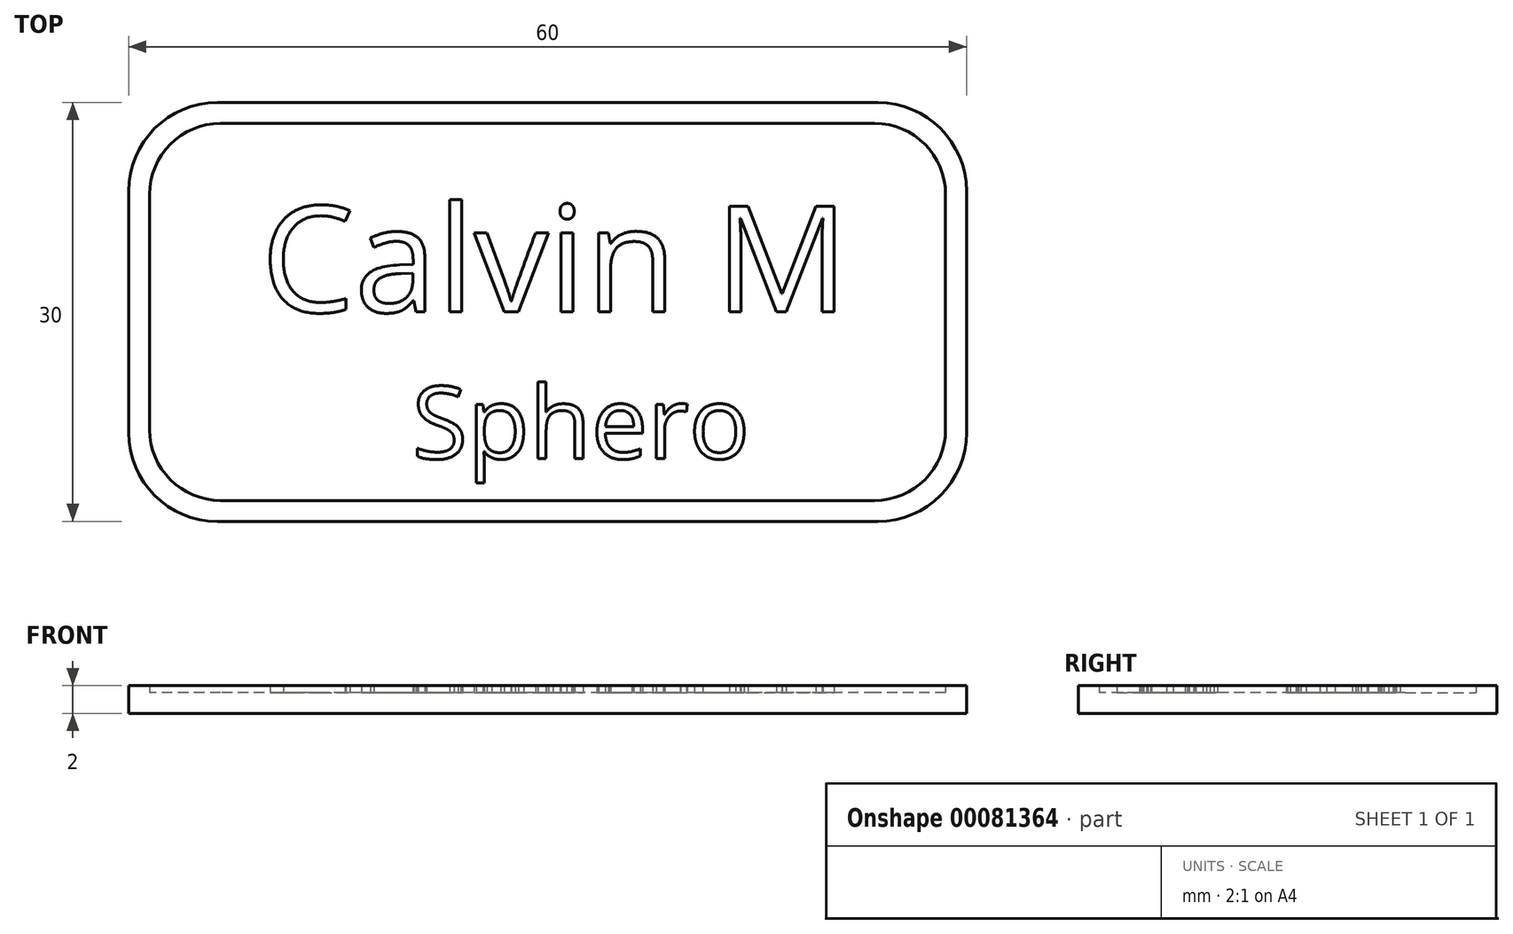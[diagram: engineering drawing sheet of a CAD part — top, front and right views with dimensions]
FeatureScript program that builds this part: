
annotation { "Feature Type Name" : "Feature", "Feature Type Description" : "" }
export const myFeature = defineFeature(function(context is Context, id is Id, definition is map)
    precondition{}
    {
        {
            var Q0;
            Q0=qCreatedBy(makeId("Top.planeOp"),FACE);
            var sketch = newSketch(context, id + "F0", { "sketchPlane" : qUnion([Q0])});
            skLineSegment(sketch, "E0.bottom", {"start": v(23.65, 15) * mm, "end": v(-23.65, 15) * mm});
            skLineSegment(sketch, "E0.top", {"start": v(23.65, -15) * mm, "end": v(-23.65, -15) * mm});
            skLineSegment(sketch, "E0.left", {"start": v(30, 8.65) * mm, "end": v(30, -8.65) * mm});
            skLineSegment(sketch, "E0.right", {"start": v(-30, 8.65) * mm, "end": v(-30, -8.65) * mm});
            skPoint(sketch, "E0.middle", {"position": v(0, 0) * mm});
            skPoint(sketch, "E1.visualSharp", {"position": v(-30, 15) * mm});
            skArc(sketch, "E1.filletArc", {"start": v(-23.65, 15) * mm, "mid": v(-28.14, 13.14) * mm, "end": v(-30, 8.65) * mm});
            skPoint(sketch, "E2.visualSharp", {"position": v(-30, -15) * mm});
            skArc(sketch, "E2.filletArc", {"start": v(-30, -8.65) * mm, "mid": v(-28.14, -13.14) * mm, "end": v(-23.65, -15) * mm});
            skPoint(sketch, "E3.visualSharp", {"position": v(30, -15) * mm});
            skArc(sketch, "E3.filletArc", {"start": v(23.65, -15) * mm, "mid": v(28.14, -13.14) * mm, "end": v(30, -8.65) * mm});
            skPoint(sketch, "E4.visualSharp", {"position": v(30, 15) * mm});
            skArc(sketch, "E4.filletArc", {"start": v(30, 8.65) * mm, "mid": v(28.14, 13.14) * mm, "end": v(23.65, 15) * mm});
            skSolve(sketch);
        }
        {
            var Q0;
            Q0 = qSketchRegion(id + "F0", true);
            extrude(context, id + "F1", {"entities" : qUnion([Q0]), "depth" : 1.5 * mm});
        }
        {
            var Q0;
            Q0=makeQuery(id+"F1.opExtrude","CAP_FACE",FACE,{"disambiguationData":[OSD([sQuery(id+"F0.wireOp",EDGE,"E0.bottom"),sQuery(id+"F0.wireOp",EDGE,"E0.top"),sQuery(id+"F0.wireOp",EDGE,"E0.left"),sQuery(id+"F0.wireOp",EDGE,"E0.right"),sQuery(id+"F0.wireOp",EDGE,"E1.filletArc"),sQuery(id+"F0.wireOp",EDGE,"E2.filletArc"),sQuery(id+"F0.wireOp",EDGE,"E3.filletArc"),sQuery(id+"F0.wireOp",EDGE,"E4.filletArc")])],"isStart":false});
            var sketch = newSketch(context, id + "F2", { "sketchPlane" : qUnion([Q0])});
            skLineSegment(sketch, "E5.bottom", {"start": v(23.42, 13.5) * mm, "end": v(-23.42, 13.5) * mm});
            skLineSegment(sketch, "E5.top", {"start": v(23.42, -13.5) * mm, "end": v(-23.42, -13.5) * mm});
            skLineSegment(sketch, "E5.left", {"start": v(28.5, 8.42) * mm, "end": v(28.5, -8.42) * mm});
            skLineSegment(sketch, "E5.right", {"start": v(-28.5, 8.42) * mm, "end": v(-28.5, -8.42) * mm});
            skPoint(sketch, "E5.middle", {"position": v(0, 0) * mm});
            skPoint(sketch, "E6.visualSharp", {"position": v(-28.5, 13.5) * mm});
            skArc(sketch, "E6.filletArc", {"start": v(-23.42, 13.5) * mm, "mid": v(-27.01, 12.01) * mm, "end": v(-28.5, 8.42) * mm});
            skPoint(sketch, "E7.visualSharp", {"position": v(28.5, 13.5) * mm});
            skArc(sketch, "E7.filletArc", {"start": v(28.5, 8.42) * mm, "mid": v(27.01, 12.01) * mm, "end": v(23.42, 13.5) * mm});
            skPoint(sketch, "E8.visualSharp", {"position": v(28.5, -13.5) * mm});
            skArc(sketch, "E8.filletArc", {"start": v(23.42, -13.5) * mm, "mid": v(27.01, -12.01) * mm, "end": v(28.5, -8.42) * mm});
            skPoint(sketch, "E9.visualSharp", {"position": v(-28.5, -13.5) * mm});
            skArc(sketch, "E9.filletArc", {"start": v(-28.5, -8.42) * mm, "mid": v(-27.01, -12.01) * mm, "end": v(-23.42, -13.5) * mm});
            skSolve(sketch);
        }
        {
            var Q0;
            Q0=makeQuery(id+"F2.imprint","IMPRINT",FACE,{"disambiguationData":[TD([[makeQuery(id+"F2.imprint","IMPRINT",EDGE,{"derivedFrom":sQuery(id+"F2.wireOp",EDGE,"E5.bottom")}),-1.0]])]});
            extrude(context, id + "F3", {"entities" : qUnion([Q0]), "operationType" : NewBodyOperationType.ADD, "depth" : .5 * mm});
        }
        {
            var Q0;
            Q0=makeQuery(id+"F1.opExtrude","CAP_FACE",FACE,{"disambiguationData":[OSD([sQuery(id+"F0.wireOp",EDGE,"E0.bottom"),sQuery(id+"F0.wireOp",EDGE,"E0.top"),sQuery(id+"F0.wireOp",EDGE,"E0.left"),sQuery(id+"F0.wireOp",EDGE,"E0.right"),sQuery(id+"F0.wireOp",EDGE,"E1.filletArc"),sQuery(id+"F0.wireOp",EDGE,"E2.filletArc"),sQuery(id+"F0.wireOp",EDGE,"E3.filletArc"),sQuery(id+"F0.wireOp",EDGE,"E4.filletArc")])],"isStart":false});
            var sketch = newSketch(context, id + "F4", { "sketchPlane" : qUnion([Q0])});
            skPoint(sketch, "E10.firstSnap0", {"position": v(0, -13.5) * mm});
            skPoint(sketch, "E11.secondSnap0", {"position": v(-28.5, 0) * mm});
            skText(sketch, "E12", { "text": "Calvin M", "fontName": "OpenSans-Regular.ttf"});
            skText(sketch, "E13", { "text": "Sphero", "fontName": "OpenSans-Regular.ttf"});
            const initialGuessF4  = {"E12": [-0.02051, 0, 1, 0, 0.00763], "E13": [-0.0097, -0.0105, 1, 0, 0.0052]};
            skSetInitialGuess(sketch, initialGuessF4);
            skSolve(sketch);
        }
        {
            var Q0;
            Q0 = qSketchRegion(id + "F4", true);
            extrude(context, id + "F5", {"entities" : qUnion([Q0]), "operationType" : NewBodyOperationType.ADD, "depth" : .5 * mm});
        }
    });
